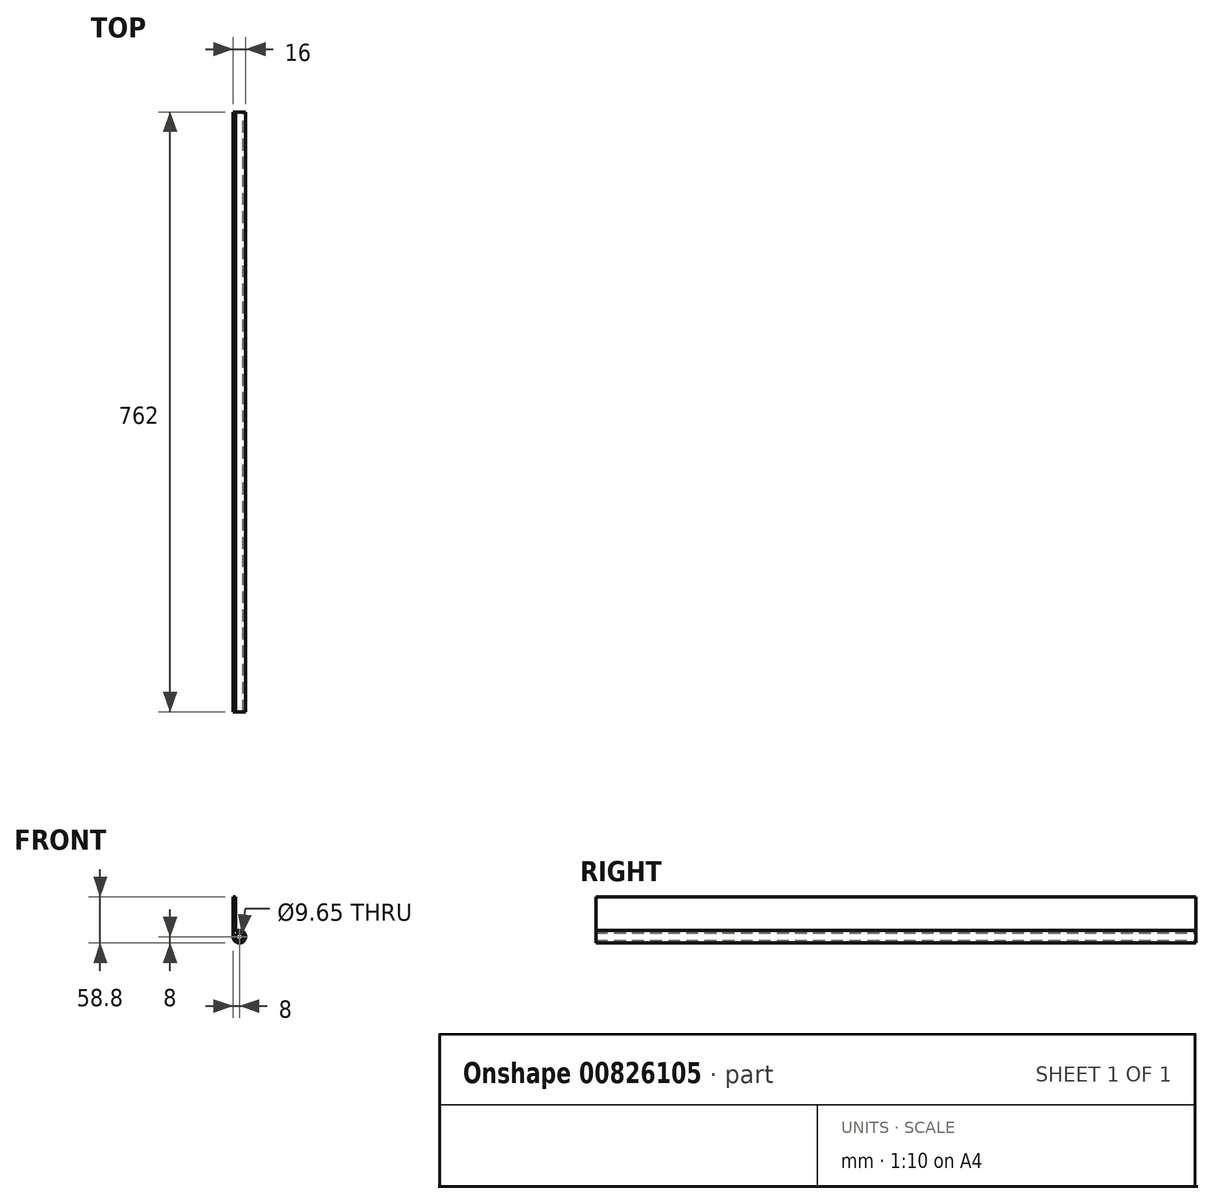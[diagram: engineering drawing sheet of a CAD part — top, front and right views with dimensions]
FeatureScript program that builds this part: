
annotation { "Feature Type Name" : "Feature", "Feature Type Description" : "" }
export const myFeature = defineFeature(function(context is Context, id is Id, definition is map)
    precondition{}
    {
        {
            var Q0;
            Q0=qCreatedBy(makeId("Front.planeOp"),FACE);
            var sketch = newSketch(context, id + "F0", { "sketchPlane" : qUnion([Q0])});
            skCircle(sketch, "E0", {"center": v(0, 0) * mm, "radius": 4.83 * mm});
            skArc(sketch, "E1.0", {"start": v(-8, 0) * mm, "mid": v(0, -8) * mm, "end": v(8, 0) * mm});
            skLineSegment(sketch, "E2", {"start": v(-8, 0) * mm, "end": v(-8, 50.8) * mm});
            skLineSegment(sketch, "E3.0", {"start": v(-4.83, 6.38) * mm, "end": v(-4.83, 50.8) * mm});
            skLineSegment(sketch, "E4", {"start": v(-8, 50.8) * mm, "end": v(-4.83, 50.8) * mm});
            skArc(sketch, "E5.trimOffspring", {"start": v(8, 0) * mm, "mid": v(3.56, 7.16) * mm, "end": v(-4.83, 6.38) * mm});
            skSolve(sketch);
        }
        {
            var Q0;
            Q0=qSketchRegion(id+"F0",true);
            extrude(context, id + "F1", {"entities" : qUnion([Q0]), "endBound" : BoundingType.SYMMETRIC, "depth" : 762 * mm, "offsetDistance" : 25.4 * mm});
        }
    });
